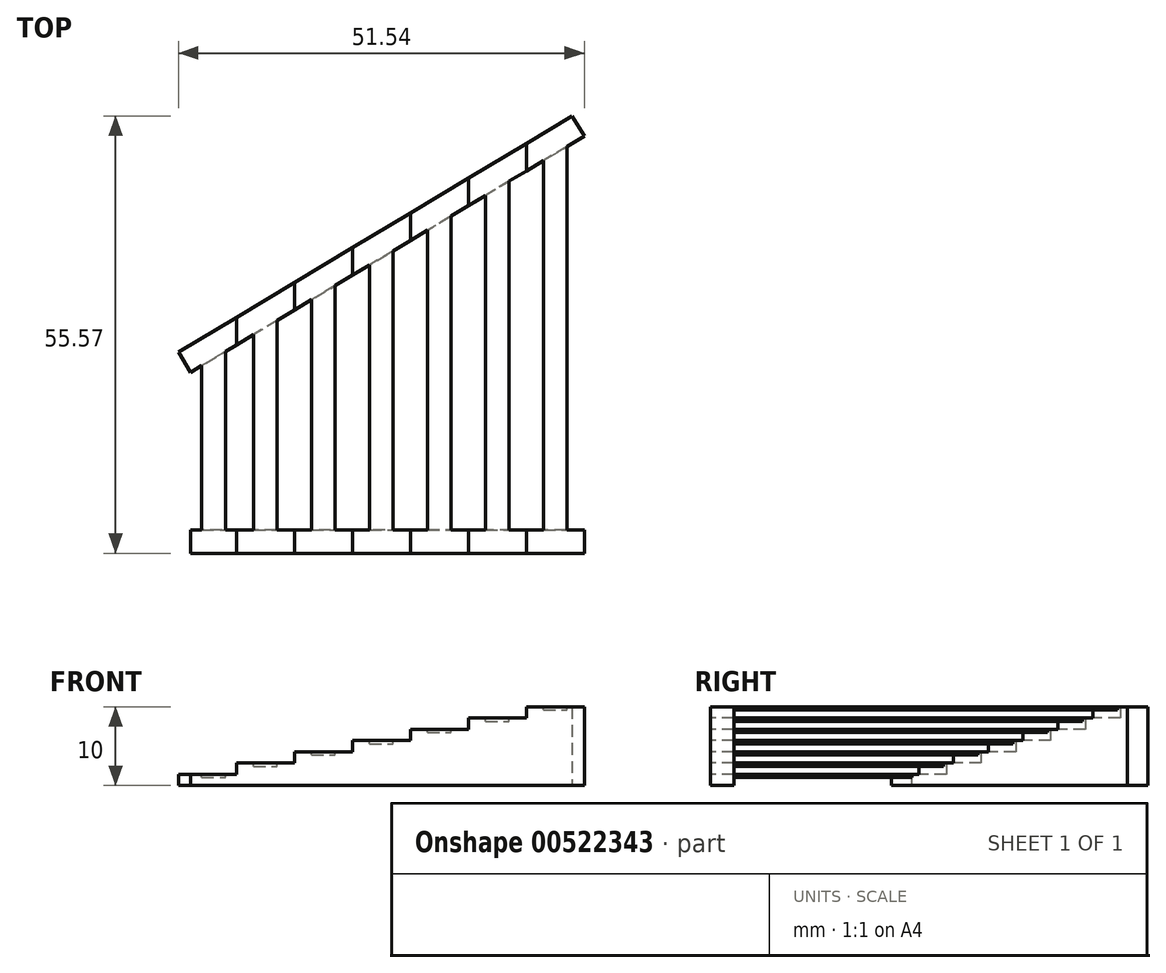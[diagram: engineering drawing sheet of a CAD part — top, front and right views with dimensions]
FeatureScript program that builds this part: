
annotation { "Feature Type Name" : "Feature", "Feature Type Description" : "" }
export const myFeature = defineFeature(function(context is Context, id is Id, definition is map)
    precondition{}
    {
        {
            var Q0;
            Q0=qCreatedBy(makeId("Top.planeOp"),FACE);
            var sketch = newSketch(context, id + "F0", { "sketchPlane" : qUnion([Q0])});
            skLineSegment(sketch, "E0.bottom", {"start": v(25, -1.5) * mm, "end": v(-25, -1.5) * mm});
            skLineSegment(sketch, "E0.top", {"start": v(25, 1.5) * mm, "end": v(-25, 1.5) * mm});
            skLineSegment(sketch, "E0.left", {"start": v(25, -1.5) * mm, "end": v(25, 1.5) * mm});
            skLineSegment(sketch, "E0.right", {"start": v(-25, -1.5) * mm, "end": v(-25, 1.5) * mm});
            skPoint(sketch, "E0.middle", {"position": v(0, 0) * mm});
            skLineSegment(sketch, "E1", {"start": v(-25, 21.5) * mm, "end": v(25, 51.5) * mm, "construction": true});
            skLineSegment(sketch, "E2.bottom", {"start": v(-25, 21.5) * mm, "end": v(25, 51.5) * mm});
            skLineSegment(sketch, "E2.top", {"start": v(-26.54, 24.07) * mm, "end": v(23.46, 54.07) * mm});
            skLineSegment(sketch, "E2.left", {"start": v(-25, 21.5) * mm, "end": v(-26.54, 24.07) * mm});
            skLineSegment(sketch, "E2.right", {"start": v(25, 51.5) * mm, "end": v(23.46, 54.07) * mm});
            skSolve(sketch);
        }
        {
            var Q0;
            Q0 = qSketchRegion(id + "F0", true);
            extrude(context, id + "F1", {"entities" : qUnion([Q0]), "depth" : 10 * mm, "offsetDistance" : 25 * mm});
        }
        {
            var Q0;
            Q0=makeQuery(id+"F1.opExtrude","SWEPT_FACE",FACE,{"disambiguationData":[OSD([sQuery(id+"F0.wireOp",EDGE,"E0.bottom")])]});
            var sketch = newSketch(context, id + "F2", { "sketchPlane" : qUnion([Q0])});
            skLineSegment(sketch, "E3", {"start": v(-26.54, 10) * mm, "end": v(-26.54, 1.43) * mm});
            skLineSegment(sketch, "E4", {"start": v(-26.54, 1.43) * mm, "end": v(-19.18, 1.43) * mm});
            skLineSegment(sketch, "E5", {"start": v(-19.18, 1.43) * mm, "end": v(-19.18, 2.86) * mm});
            skLineSegment(sketch, "E6", {"start": v(-19.18, 2.86) * mm, "end": v(-11.82, 2.86) * mm});
            skLineSegment(sketch, "E7", {"start": v(-11.82, 2.86) * mm, "end": v(-11.82, 4.29) * mm});
            skLineSegment(sketch, "E8", {"start": v(-11.82, 4.29) * mm, "end": v(-4.45, 4.29) * mm});
            skLineSegment(sketch, "E9", {"start": v(-4.45, 4.29) * mm, "end": v(-4.45, 5.71) * mm});
            skLineSegment(sketch, "E10", {"start": v(-4.45, 5.71) * mm, "end": v(2.9, 5.71) * mm});
            skLineSegment(sketch, "E11", {"start": v(2.9, 5.71) * mm, "end": v(2.9, 7.14) * mm});
            skLineSegment(sketch, "E12", {"start": v(2.9, 7.14) * mm, "end": v(10.27, 7.14) * mm});
            skLineSegment(sketch, "E13", {"start": v(10.27, 7.14) * mm, "end": v(10.27, 8.57) * mm});
            skLineSegment(sketch, "E14", {"start": v(10.27, 8.57) * mm, "end": v(17.64, 8.57) * mm});
            skLineSegment(sketch, "E15", {"start": v(17.64, 8.57) * mm, "end": v(17.64, 10) * mm});
            skLineSegment(sketch, "E16", {"start": v(-26.54, 10) * mm, "end": v(17.64, 10) * mm});
            skLineSegment(sketch, "E17", {"start": v(-22.86, 1.43) * mm, "end": v(-22.86, 0) * mm, "construction": true});
            skLineSegment(sketch, "E18", {"start": v(17.64, 9.29) * mm, "end": v(25, 9.29) * mm, "construction": true});
            skSolve(sketch);
        }
        {
            var Q0;
            Q0 = qSketchRegion(id + "F2", true);
            extrude(context, id + "F3", {"entities" : qUnion([Q0]), "operationType" : NewBodyOperationType.REMOVE, "endBound" : BoundingType.THROUGH_ALL, "oppositeDirection" : true, "depth" : 25 * mm, "offsetDistance" : 25 * mm});
        }
        {
            var Q0;
            Q0=makeQuery(id+"F1.opExtrude","SWEPT_FACE",FACE,{"disambiguationData":[OSD([sQuery(id+"F0.wireOp",EDGE,"E0.bottom")])]});
            var sketch = newSketch(context, id + "F4", { "sketchPlane" : qUnion([Q0])});
            skLineSegment(sketch, "E19.bottom", {"start": v(-23.6, 1.03) * mm, "end": v(-20.6, 1.03) * mm});
            skLineSegment(sketch, "E19.top", {"start": v(-23.6, 1.43) * mm, "end": v(-20.6, 1.43) * mm});
            skLineSegment(sketch, "E19.left", {"start": v(-23.6, 1.03) * mm, "end": v(-23.6, 1.43) * mm});
            skLineSegment(sketch, "E19.right", {"start": v(-20.6, 1.03) * mm, "end": v(-20.6, 1.43) * mm});
            skLineSegment(sketch, "E20.bottom", {"start": v(-17, 2.46) * mm, "end": v(-14, 2.46) * mm});
            skLineSegment(sketch, "E20.top", {"start": v(-17, 2.86) * mm, "end": v(-14, 2.86) * mm});
            skLineSegment(sketch, "E20.left", {"start": v(-17, 2.46) * mm, "end": v(-17, 2.86) * mm});
            skLineSegment(sketch, "E20.right", {"start": v(-14, 2.46) * mm, "end": v(-14, 2.86) * mm});
            skLineSegment(sketch, "E21.bottom", {"start": v(-9.64, 3.89) * mm, "end": v(-6.64, 3.89) * mm});
            skLineSegment(sketch, "E21.top", {"start": v(-9.64, 4.29) * mm, "end": v(-6.64, 4.29) * mm});
            skLineSegment(sketch, "E21.left", {"start": v(-9.64, 3.89) * mm, "end": v(-9.64, 4.29) * mm});
            skLineSegment(sketch, "E21.right", {"start": v(-6.64, 3.89) * mm, "end": v(-6.64, 4.29) * mm});
            skLineSegment(sketch, "E22.bottom", {"start": v(-2.27, 5.31) * mm, "end": v(0.73, 5.31) * mm});
            skLineSegment(sketch, "E22.top", {"start": v(-2.27, 5.71) * mm, "end": v(0.73, 5.71) * mm});
            skLineSegment(sketch, "E22.left", {"start": v(-2.27, 5.31) * mm, "end": v(-2.27, 5.71) * mm});
            skLineSegment(sketch, "E22.right", {"start": v(0.73, 5.31) * mm, "end": v(0.73, 5.71) * mm});
            skLineSegment(sketch, "E23.bottom", {"start": v(5.1, 6.74) * mm, "end": v(8.1, 6.74) * mm});
            skLineSegment(sketch, "E23.top", {"start": v(5.1, 7.14) * mm, "end": v(8.1, 7.14) * mm});
            skLineSegment(sketch, "E23.left", {"start": v(5.1, 6.74) * mm, "end": v(5.1, 7.14) * mm});
            skLineSegment(sketch, "E23.right", {"start": v(8.1, 6.74) * mm, "end": v(8.1, 7.14) * mm});
            skLineSegment(sketch, "E24.bottom", {"start": v(12.45, 8.17) * mm, "end": v(15.45, 8.17) * mm});
            skLineSegment(sketch, "E24.top", {"start": v(12.45, 8.57) * mm, "end": v(15.45, 8.57) * mm});
            skLineSegment(sketch, "E24.left", {"start": v(12.45, 8.17) * mm, "end": v(12.45, 8.57) * mm});
            skLineSegment(sketch, "E24.right", {"start": v(15.45, 8.17) * mm, "end": v(15.45, 8.57) * mm});
            skLineSegment(sketch, "E25.bottom", {"start": v(19.82, 9.6) * mm, "end": v(22.82, 9.6) * mm});
            skLineSegment(sketch, "E25.top", {"start": v(19.82, 10) * mm, "end": v(22.82, 10) * mm});
            skLineSegment(sketch, "E25.left", {"start": v(19.82, 9.6) * mm, "end": v(19.82, 10) * mm});
            skLineSegment(sketch, "E25.right", {"start": v(22.82, 9.6) * mm, "end": v(22.82, 10) * mm});
            skPoint(sketch, "E26", {"position": v(21.32, 10) * mm});
            skPoint(sketch, "E27", {"position": v(-22.1, 1.43) * mm});
            skPoint(sketch, "E28", {"position": v(-15.5, 2.86) * mm});
            skPoint(sketch, "E29", {"position": v(-8.14, 4.29) * mm});
            skPoint(sketch, "E30", {"position": v(-0.77, 5.71) * mm});
            skPoint(sketch, "E31", {"position": v(6.6, 7.14) * mm});
            skPoint(sketch, "E32", {"position": v(13.95, 8.57) * mm});
            skSolve(sketch);
        }
        {
            var Q0;
            Q0 = qSketchRegion(id + "F4", true);
            var Q1;
            Q1=makeQuery(id+"F1.opExtrude","SWEPT_FACE",FACE,{"disambiguationData":[OSD([sQuery(id+"F0.wireOp",EDGE,"E2.top")])]});
            var Q2;
            Q2=makeQuery(id+"F1.opExtrude","SWEPT_BODY",BODY,{"disambiguationData":[OSD([sQuery(id+"F0.wireOp",EDGE,"E2.bottom"),sQuery(id+"F0.wireOp",EDGE,"E2.top"),sQuery(id+"F0.wireOp",EDGE,"E2.left"),sQuery(id+"F0.wireOp",EDGE,"E2.right")])]});
            extrude(context, id + "F5", {"entities" : qUnion([Q0]), "operationType" : NewBodyOperationType.ADD, "endBound" : BoundingType.UP_TO_SURFACE, "oppositeDirection" : true, "depth" : 25 * mm, "endBoundEntityFace" : qUnion([Q1]), "endBoundEntityBody" : qUnion([Q2]), "offsetDistance" : 25 * mm});
        }
    });
